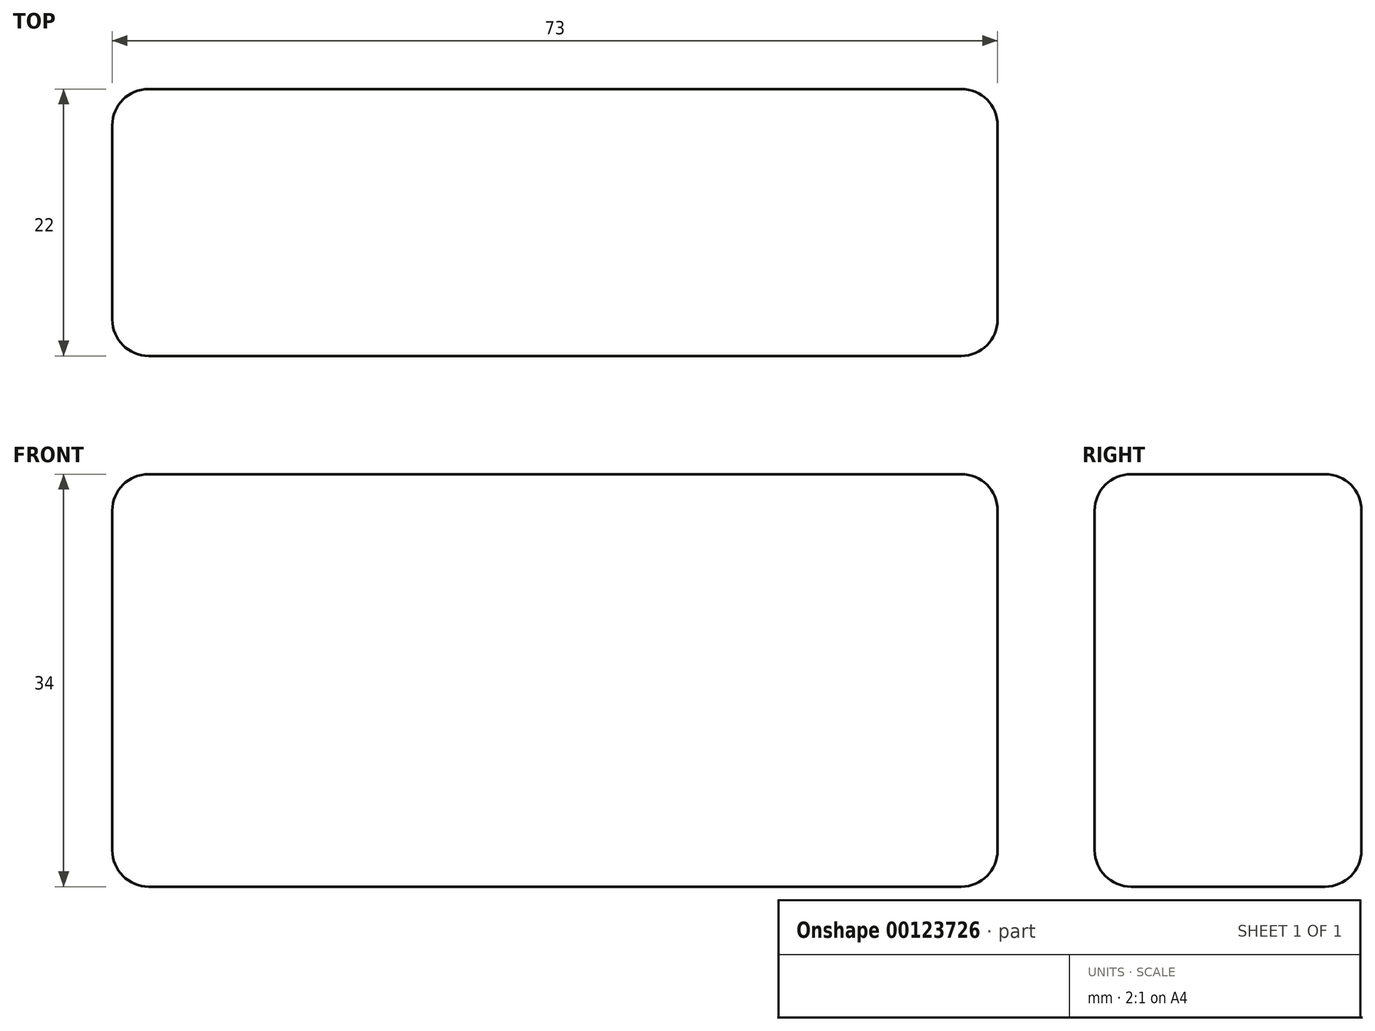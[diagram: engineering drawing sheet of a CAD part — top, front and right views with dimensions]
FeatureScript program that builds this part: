
annotation { "Feature Type Name" : "Feature", "Feature Type Description" : "" }
export const myFeature = defineFeature(function(context is Context, id is Id, definition is map)
    precondition{}
    {
        {
            var Q0;
            Q0=qCreatedBy(makeId("Top.planeOp"),FACE);
            var Q1;
            Q1=qCreatedBy(makeId("Top.planeOp"),FACE);
            var sketch = newSketch(context, id + "F0", { "sketchPlane" : qUnion([Q0, Q1])});
            skLineSegment(sketch, "E0.bottom", {"start": v(-33.5, 11) * mm, "end": v(33.5, 11) * mm});
            skLineSegment(sketch, "E0.top", {"start": v(-33.5, -11) * mm, "end": v(33.5, -11) * mm});
            skLineSegment(sketch, "E0.left", {"start": v(-36.5, 8) * mm, "end": v(-36.5, -8) * mm});
            skLineSegment(sketch, "E0.right", {"start": v(36.5, 8) * mm, "end": v(36.5, -8) * mm});
            skPoint(sketch, "E1.visualSharp", {"position": v(-36.5, 11) * mm});
            skArc(sketch, "E1.filletArc", {"start": v(-33.5, 11) * mm, "mid": v(-35.62, 10.12) * mm, "end": v(-36.5, 8) * mm});
            skPoint(sketch, "E2.visualSharp", {"position": v(-36.5, -11) * mm});
            skArc(sketch, "E2.filletArc", {"start": v(-36.5, -8) * mm, "mid": v(-35.62, -10.12) * mm, "end": v(-33.5, -11) * mm});
            skPoint(sketch, "E3.visualSharp", {"position": v(36.5, -11) * mm});
            skArc(sketch, "E3.filletArc", {"start": v(33.5, -11) * mm, "mid": v(35.62, -10.12) * mm, "end": v(36.5, -8) * mm});
            skPoint(sketch, "E4.visualSharp", {"position": v(36.5, 11) * mm});
            skArc(sketch, "E4.filletArc", {"start": v(36.5, 8) * mm, "mid": v(35.62, 10.12) * mm, "end": v(33.5, 11) * mm});
            skSolve(sketch);
        }
        {
            var Q0;
            Q0=qSketchRegion(id+"F0",true);
            extrude(context, id + "F1", {"entities" : qUnion([Q0]), "depth" : 34 * mm});
        }
        {
            var Q0;
            Q0=makeQuery(id+"F1.opExtrude","CAP_FACE",FACE,{"disambiguationData":[OSD([sQuery(id+"F0.wireOp",EDGE,"E0.bottom"),sQuery(id+"F0.wireOp",EDGE,"E0.top"),sQuery(id+"F0.wireOp",EDGE,"E0.left"),sQuery(id+"F0.wireOp",EDGE,"E0.right"),sQuery(id+"F0.wireOp",EDGE,"E1.filletArc"),sQuery(id+"F0.wireOp",EDGE,"E2.filletArc"),sQuery(id+"F0.wireOp",EDGE,"E3.filletArc"),sQuery(id+"F0.wireOp",EDGE,"E4.filletArc")])],"isStart":true});
            var Q1;
            Q1=makeQuery(id+"F1.opExtrude","CAP_FACE",FACE,{"disambiguationData":[OSD([sQuery(id+"F0.wireOp",EDGE,"E0.bottom"),sQuery(id+"F0.wireOp",EDGE,"E0.top"),sQuery(id+"F0.wireOp",EDGE,"E0.left"),sQuery(id+"F0.wireOp",EDGE,"E0.right"),sQuery(id+"F0.wireOp",EDGE,"E1.filletArc"),sQuery(id+"F0.wireOp",EDGE,"E2.filletArc"),sQuery(id+"F0.wireOp",EDGE,"E3.filletArc"),sQuery(id+"F0.wireOp",EDGE,"E4.filletArc")])],"isStart":false});
            fillet(context, id + "F2", {"entities" : qUnion([Q0, Q1]), "radius" : 3 * mm, "tangentPropagation" : true, "allowEdgeOverflow" : false});
        }
    });
